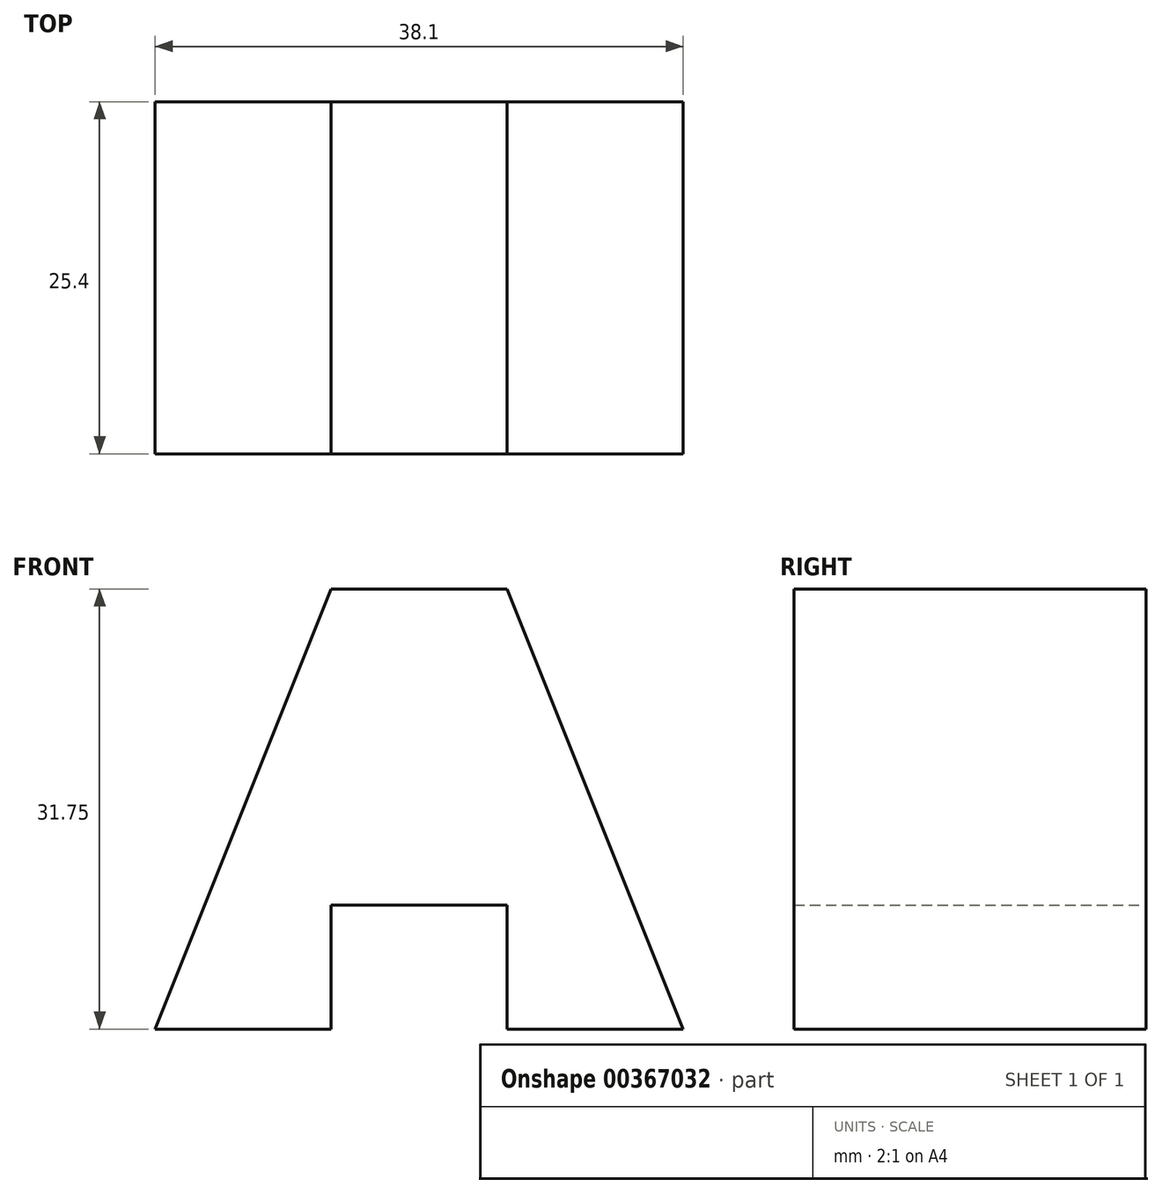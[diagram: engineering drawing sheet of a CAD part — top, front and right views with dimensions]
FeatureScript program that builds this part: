
annotation { "Feature Type Name" : "Feature", "Feature Type Description" : "" }
export const myFeature = defineFeature(function(context is Context, id is Id, definition is map)
    precondition{}
    {
        {
            var Q0;
            Q0=qCreatedBy(makeId("Front.planeOp"),FACE);
            var sketch = newSketch(context, id + "F0", { "sketchPlane" : qUnion([Q0])});
            skLineSegment(sketch, "E0", {"start": v(0, 0) * mm, "end": v(12.7, 0) * mm});
            skLineSegment(sketch, "E1", {"start": v(12.7, 0) * mm, "end": v(12.7, 8.95) * mm});
            skLineSegment(sketch, "E2", {"start": v(12.7, 8.95) * mm, "end": v(25.4, 8.95) * mm});
            skLineSegment(sketch, "E3", {"start": v(25.4, 8.95) * mm, "end": v(25.4, 0) * mm});
            skLineSegment(sketch, "E4", {"start": v(25.4, 0) * mm, "end": v(38.1, 0) * mm});
            skLineSegment(sketch, "E5", {"start": v(38.1, 0) * mm, "end": v(25.4, 31.75) * mm});
            skLineSegment(sketch, "E6", {"start": v(25.4, 31.75) * mm, "end": v(12.7, 31.75) * mm});
            skLineSegment(sketch, "E7", {"start": v(12.7, 31.75) * mm, "end": v(0, 0) * mm});
            skSolve(sketch);
        }
        {
            var Q0;
            Q0=makeQuery(id+"F0.imprint","IMPRINT",FACE,{"disambiguationData":[TD([[makeQuery(id+"F0.imprint","IMPRINT",EDGE,{"derivedFrom":sQuery(id+"F0.wireOp",EDGE,"E0")}),1.0]])]});
            extrude(context, id + "F1", {"entities" : qUnion([Q0]), "depth" : 25.4 * mm});
        }
    });
